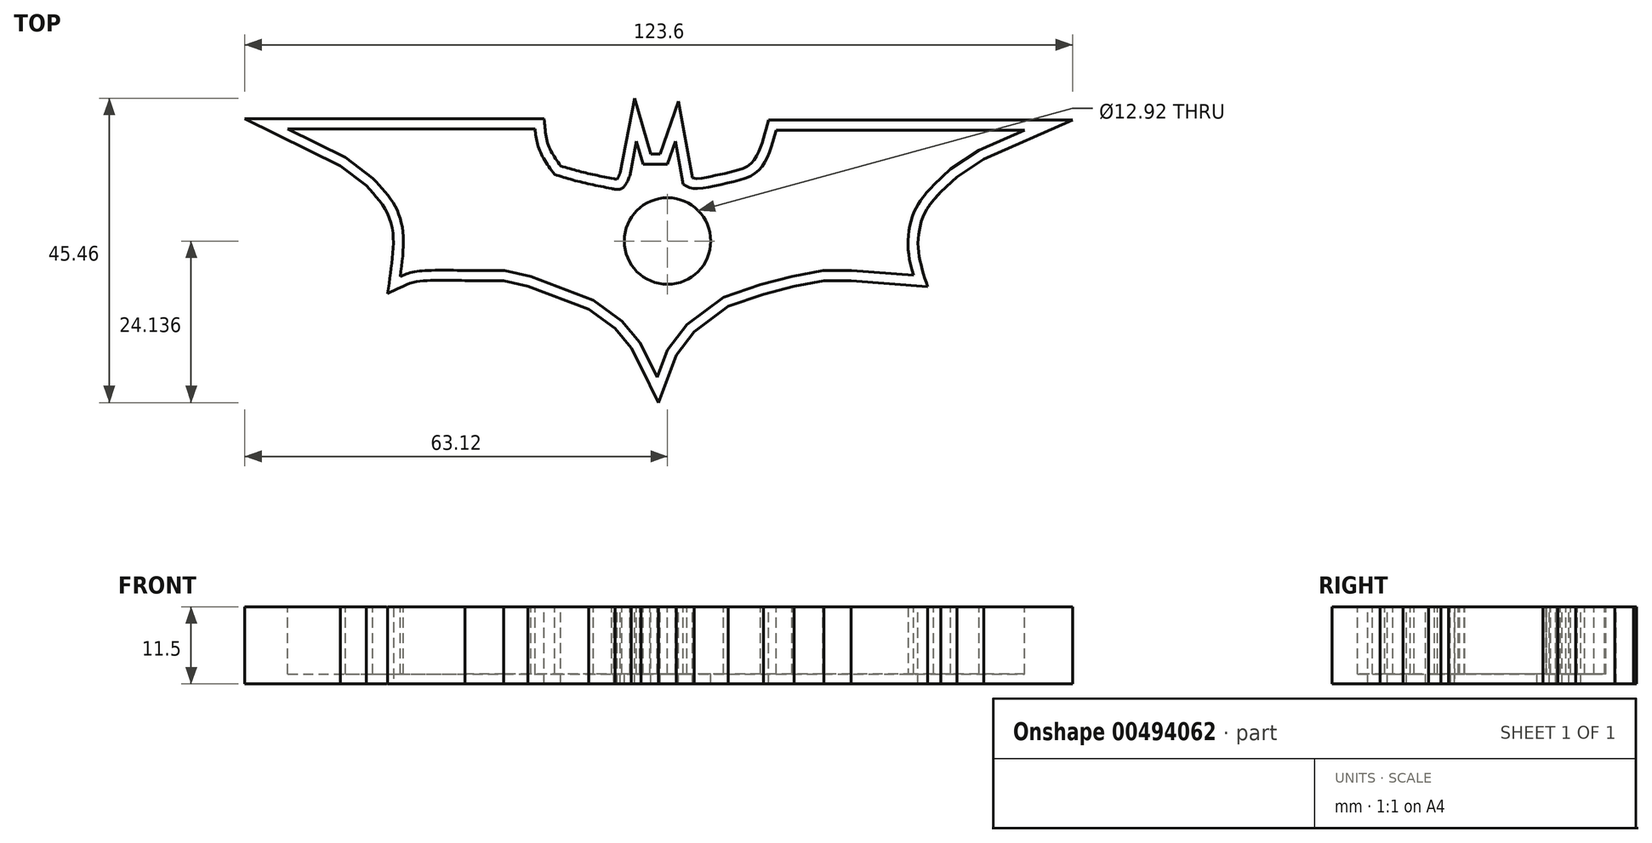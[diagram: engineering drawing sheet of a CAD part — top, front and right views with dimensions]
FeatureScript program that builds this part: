
annotation { "Feature Type Name" : "Feature", "Feature Type Description" : "" }
export const myFeature = defineFeature(function(context is Context, id is Id, definition is map)
    precondition{}
    {
        {
            var Q0;
            Q0=qCreatedBy(makeId("Top.planeOp"),FACE);
            var sketch = newSketch(context, id + "F0", { "sketchPlane" : qUnion([Q0])});
            skLineSegment(sketch, "E0", {"start": v(-56.7, 34.88) * mm, "end": v(-19.78, 34.88) * mm});
            skLineSegment(sketch, "E1", {"start": v(-4.63, 33.07) * mm, "end": v(-3.63, 29.62) * mm});
            skLineSegment(sketch, "E2", {"start": v(-3.63, 29.62) * mm, "end": v(0, 29.62) * mm});
            skLineSegment(sketch, "E3", {"start": v(0, 29.62) * mm, "end": v(1.17, 33.07) * mm});
            skLineSegment(sketch, "E4", {"start": v(1.17, 33.07) * mm, "end": v(2.35, 26.63) * mm});
            skLineSegment(sketch, "E5", {"start": v(-4.63, 33.07) * mm, "end": v(-5.63, 27.9) * mm});
            skLineSegment(sketch, "E6", {"start": v(16.23, 34.7) * mm, "end": v(53.34, 34.7) * mm});
            skLineSegment(sketch, "E7", {"start": v(36.74, 13.02) * mm, "end": v(27.48, 13.75) * mm});
            skLineSegment(sketch, "E8", {"start": v(27.48, 13.75) * mm, "end": v(23.22, 13.75) * mm});
            skLineSegment(sketch, "E9", {"start": v(23.22, 13.75) * mm, "end": v(18.6, 12.84) * mm});
            skLineSegment(sketch, "E10", {"start": v(18.6, 12.84) * mm, "end": v(13.88, 11.66) * mm});
            skLineSegment(sketch, "E11", {"start": v(13.88, 11.66) * mm, "end": v(8.34, 9.75) * mm});
            skLineSegment(sketch, "E12", {"start": v(8.34, 9.75) * mm, "end": v(2.9, 5.67) * mm});
            skLineSegment(sketch, "E13", {"start": v(2.9, 5.67) * mm, "end": v(0, 1.86) * mm});
            skLineSegment(sketch, "E14", {"start": v(0, 1.86) * mm, "end": v(-1.55, -2.22) * mm});
            skLineSegment(sketch, "E15", {"start": v(-1.55, -2.22) * mm, "end": v(-2.64, 0) * mm});
            skLineSegment(sketch, "E16", {"start": v(-2.64, 0) * mm, "end": v(-4.18, 3.04) * mm});
            skLineSegment(sketch, "E17", {"start": v(-4.18, 3.04) * mm, "end": v(-6.8, 6.22) * mm});
            skLineSegment(sketch, "E18", {"start": v(-6.8, 6.22) * mm, "end": v(-11.07, 9.3) * mm});
            skLineSegment(sketch, "E19", {"start": v(-11.07, 9.3) * mm, "end": v(-15.67, 11.04) * mm});
            skLineSegment(sketch, "E20", {"start": v(-15.67, 11.04) * mm, "end": v(-20.4, 12.84) * mm});
            skLineSegment(sketch, "E21", {"start": v(-20.4, 12.84) * mm, "end": v(-24.32, 13.75) * mm});
            skLineSegment(sketch, "E22", {"start": v(-24.32, 13.75) * mm, "end": v(-30.22, 13.75) * mm});
            skLineSegment(sketch, "E23", {"start": v(-56.7, 34.88) * mm, "end": v(-48.1, 30.62) * mm});
            skLineSegment(sketch, "E24", {"start": v(-48.1, 30.62) * mm, "end": v(-44, 27.54) * mm});
            skLineSegment(sketch, "E25", {"start": v(53.34, 34.7) * mm, "end": v(46.54, 31.7) * mm});
            skLineSegment(sketch, "E26", {"start": v(46.54, 31.7) * mm, "end": v(42.27, 28.9) * mm});
            skLineSegment(sketch, "E27", {"start": v(42.27, 28.9) * mm, "end": v(39.73, 26.54) * mm});
            skFitSpline(sketch, "E28", {"points": [v(-44, 27.54) * mm, v(-40.83, 23.63) * mm, v(-39.47, 19) * mm, v(-39.92, 12.84) * mm], "startDerivative": vector(10.94, -11.53) * mm, "endDerivative": vector(-2.44, -17.73) * mm});
            skFitSpline(sketch, "E29", {"points": [v(-19.78, 34.88) * mm, v(-19.15, 31.8) * mm, v(-16.88, 28.08) * mm], "startDerivative": vector(0.74, -6.67) * mm, "endDerivative": vector(4.96, -6.93) * mm});
            skFitSpline(sketch, "E30", {"points": [v(2.35, 26.63) * mm, v(3.99, 26) * mm, v(8.16, 26.63) * mm, v(12.79, 28.08) * mm, v(14.87, 30.62) * mm, v(16.23, 34.7) * mm], "startDerivative": vector(10.24, -6.04) * mm, "endDerivative": vector(5.48, 19.69) * mm});
            skFitSpline(sketch, "E31", {"points": [v(39.73, 26.54) * mm, v(38.7, 25.38) * mm, v(37.1, 23.1) * mm, v(35.92, 18.37) * mm, v(36.74, 13.02) * mm], "startDerivative": vector(-9.24, -10.19) * mm, "endDerivative": vector(6.1, -20.04) * mm});
            skFitSpline(sketch, "E32", {"points": [v(-8.35, 26) * mm, v(-6.8, 26) * mm, v(-5.63, 27.9) * mm], "startDerivative": vector(3.68, -0.8) * mm, "endDerivative": vector(1.82, 4.44) * mm});
            skFitSpline(sketch, "E33", {"points": [v(-39.92, 12.84) * mm, v(-37.75, 13.56) * mm, v(-30.22, 13.75) * mm], "startDerivative": vector(5.13, 2.35) * mm, "endDerivative": vector(13.48, -0.29) * mm});
            skFitSpline(sketch, "E34", {"points": [v(-16.88, 28.08) * mm, v(-13.07, 27) * mm, v(-8.35, 26) * mm], "startDerivative": vector(7.78, -2.38) * mm, "endDerivative": vector(9.25, -1.8) * mm});
            skSolve(sketch);
        }
        {
            var Q0;
            Q0=makeQuery(id+"F0.imprint","IMPRINT",FACE,{"disambiguationData":[TD([[makeQuery(id+"F0.imprint","IMPRINT",EDGE,{"derivedFrom":sQuery(id+"F0.wireOp",EDGE,"E0")}),-1.0]])]});
            extrude(context, id + "F1", {"entities" : qUnion([Q0]), "oppositeDirection" : true, "depth" : 10 * mm});
        }
        {
            var Q0;
            Q0=makeQuery(id+"F1.opExtrude","CAP_FACE",FACE,{"disambiguationData":[OSD([sQuery(id+"F0.wireOp",EDGE,"E0"),sQuery(id+"F0.wireOp",EDGE,"E1"),sQuery(id+"F0.wireOp",EDGE,"E2"),sQuery(id+"F0.wireOp",EDGE,"E3"),sQuery(id+"F0.wireOp",EDGE,"E4"),sQuery(id+"F0.wireOp",EDGE,"E5"),sQuery(id+"F0.wireOp",EDGE,"E6"),sQuery(id+"F0.wireOp",EDGE,"E7"),sQuery(id+"F0.wireOp",EDGE,"E8"),sQuery(id+"F0.wireOp",EDGE,"E9"),sQuery(id+"F0.wireOp",EDGE,"E10"),sQuery(id+"F0.wireOp",EDGE,"E11"),sQuery(id+"F0.wireOp",EDGE,"E12"),sQuery(id+"F0.wireOp",EDGE,"E13"),sQuery(id+"F0.wireOp",EDGE,"E14"),sQuery(id+"F0.wireOp",EDGE,"E15"),sQuery(id+"F0.wireOp",EDGE,"E16"),sQuery(id+"F0.wireOp",EDGE,"E17"),sQuery(id+"F0.wireOp",EDGE,"E18"),sQuery(id+"F0.wireOp",EDGE,"E19"),sQuery(id+"F0.wireOp",EDGE,"E20"),sQuery(id+"F0.wireOp",EDGE,"E21"),sQuery(id+"F0.wireOp",EDGE,"E22"),sQuery(id+"F0.wireOp",EDGE,"E23"),sQuery(id+"F0.wireOp",EDGE,"E24"),sQuery(id+"F0.wireOp",EDGE,"E25"),sQuery(id+"F0.wireOp",EDGE,"E26"),sQuery(id+"F0.wireOp",EDGE,"E27"),sQuery(id+"F0.wireOp",EDGE,"E28"),sQuery(id+"F0.wireOp",EDGE,"E29"),sQuery(id+"F0.wireOp",EDGE,"E30"),sQuery(id+"F0.wireOp",EDGE,"E31"),sQuery(id+"F0.wireOp",EDGE,"E32"),sQuery(id+"F0.wireOp",EDGE,"E33"),sQuery(id+"F0.wireOp",EDGE,"E34")])],"isStart":true});
            shell(context, id + "F2", {"entities" : qUnion([Q0]), "thickness" : 1.5 * mm, "oppositeDirection" : true});
        }
        {
            var Q0;
            Q0=qCreatedBy(makeId("Top.planeOp"),FACE);
            var sketch = newSketch(context, id + "F3", { "sketchPlane" : qUnion([Q0])});
            skCircle(sketch, "E35", {"center": v(0, 18.15) * mm, "radius": 6.46 * mm});
            skSolve(sketch);
        }
        {
            var Q0;
            Q0=makeQuery(id+"F3.imprint","IMPRINT",FACE,{"disambiguationData":[TD([[makeQuery(id+"F3.imprint","IMPRINT",EDGE,{"derivedFrom":sQuery(id+"F3.wireOp",EDGE,"E35")}),1.0]])]});
            extrude(context, id + "F4", {"entities" : qUnion([Q0]), "operationType" : NewBodyOperationType.REMOVE, "oppositeDirection" : true, "depth" : 25.4 * mm});
        }
    });
